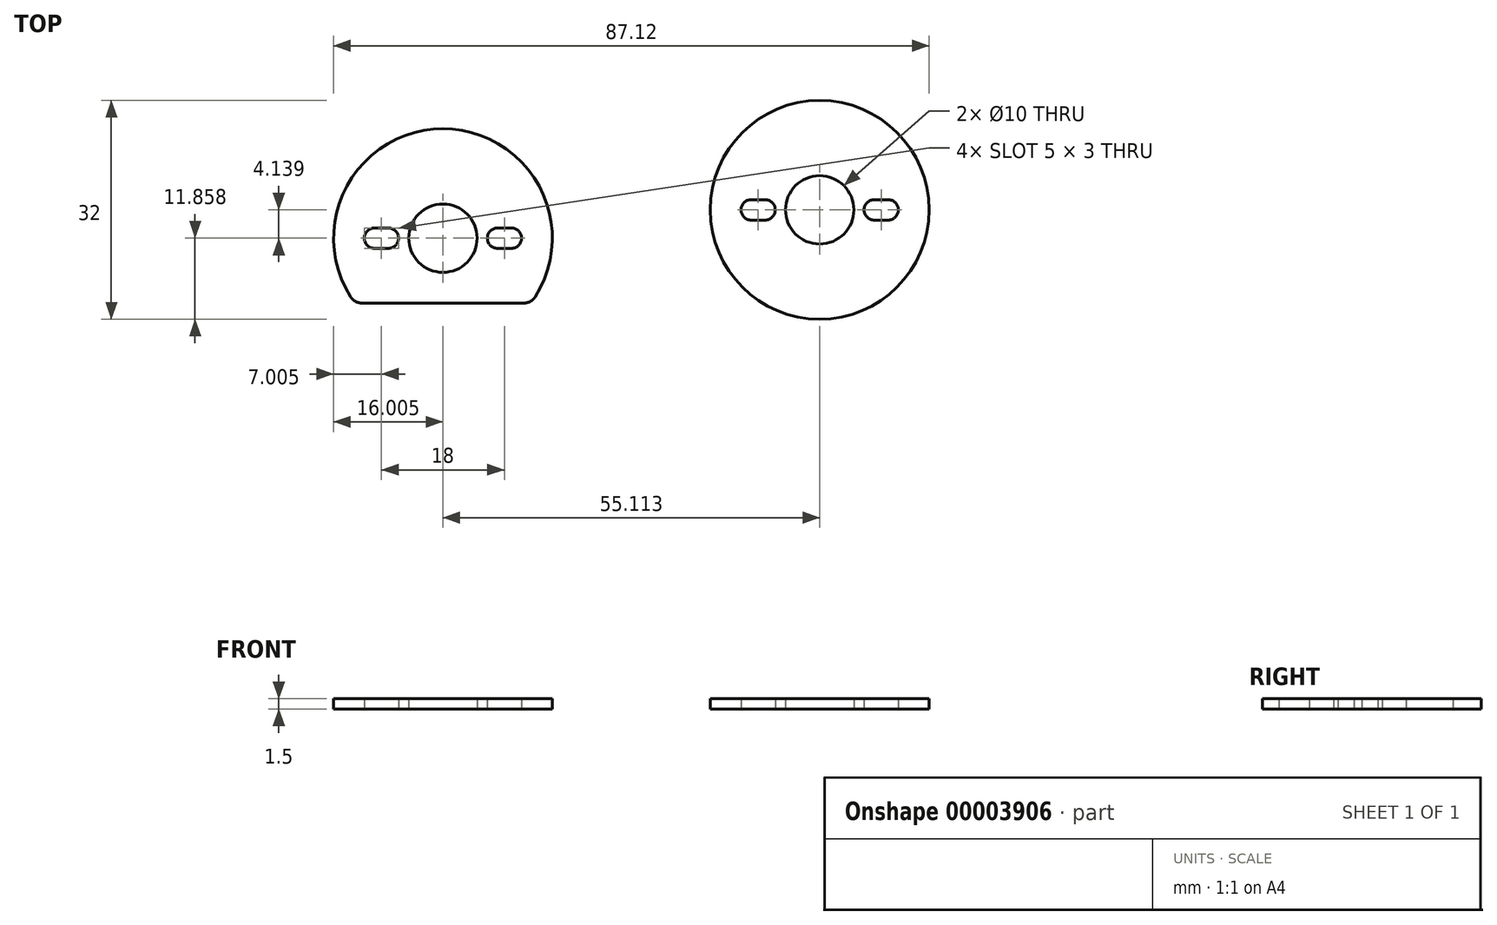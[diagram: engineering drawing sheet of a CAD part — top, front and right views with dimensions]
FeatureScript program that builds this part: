
annotation { "Feature Type Name" : "Feature", "Feature Type Description" : "" }
export const myFeature = defineFeature(function(context is Context, id is Id, definition is map)
    precondition{}
    {
        {
            var Q0;
            Q0=qCreatedBy(makeId("Top.planeOp"),FACE);
            var sketch = newSketch(context, id + "F0", { "sketchPlane" : qUnion([Q0])});
            skCircle(sketch, "E0", {"center": v(-43.17, 52.27) * mm, "radius": 5 * mm});
            skCircle(sketch, "E1", {"center": v(-35.17, 52.27) * mm, "radius": 1.5 * mm});
            skCircle(sketch, "E2", {"center": v(-33.17, 52.27) * mm, "radius": 1.5 * mm});
            skCircle(sketch, "E3", {"center": v(-51.17, 52.27) * mm, "radius": 1.5 * mm});
            skCircle(sketch, "E4", {"center": v(-53.17, 52.27) * mm, "radius": 1.5 * mm});
            skLineSegment(sketch, "E5", {"start": v(-31.41, 53.77) * mm, "end": v(-37.4, 53.77) * mm});
            skLineSegment(sketch, "E6", {"start": v(-36.75, 50.77) * mm, "end": v(-31.2, 50.77) * mm});
            skLineSegment(sketch, "E7", {"start": v(-49.7, 50.77) * mm, "end": v(-55.41, 50.77) * mm});
            skLineSegment(sketch, "E8", {"start": v(-55.27, 53.77) * mm, "end": v(-48.63, 53.77) * mm});
            skLineSegment(sketch, "E9", {"start": v(-54.99, 42.77) * mm, "end": v(-31.34, 42.77) * mm});
            skArc(sketch, "E10", {"start": v(-29.66, 43.7) * mm, "mid": v(-43.17, 68.27) * mm, "end": v(-56.68, 43.7) * mm});
            skArc(sketch, "E11.filletArc", {"start": v(-56.68, 43.7) * mm, "mid": v(-55.95, 43.02) * mm, "end": v(-54.99, 42.77) * mm});
            skArc(sketch, "E12.filletArc", {"start": v(-31.34, 42.77) * mm, "mid": v(-30.38, 43.02) * mm, "end": v(-29.66, 43.7) * mm});
            skSolve(sketch);
        }
        {
            var Q0;
            Q0=makeQuery(id+"F0.imprint","IMPRINT",FACE,{"disambiguationData":[TD([[makeQuery(id+"F0.imprint","IMPRINT",EDGE,{"derivedFrom":sQuery(id+"F0.wireOp",EDGE,"E0")}),-1.0]])]});
            extrude(context, id + "F1", {"entities" : qUnion([Q0]), "depth" : 1.5 * mm});
        }
        {
            var Q0;
            Q0=qCreatedBy(makeId("Top.planeOp"),FACE);
            var sketch = newSketch(context, id + "F2", { "sketchPlane" : qUnion([Q0])});
            skCircle(sketch, "E13", {"center": v(11.95, 56.4) * mm, "radius": 5 * mm});
            skArc(sketch, "E14", {"start": v(-1.56, 64.98) * mm, "mid": v(-2.98, 50.64) * mm, "end": v(7.7, 40.98) * mm});
            skArc(sketch, "E15", {"start": v(16.19, 40.98) * mm, "mid": v(26.87, 50.64) * mm, "end": v(25.46, 64.98) * mm});
            skLineSegment(sketch, "E16", {"start": v(15.66, 40.9) * mm, "end": v(8.24, 40.9) * mm});
            skLineSegment(sketch, "E17", {"start": v(0.13, 65.9) * mm, "end": v(23.77, 65.9) * mm});
            skCircle(sketch, "E18", {"center": v(19.95, 56.4) * mm, "radius": 1.5 * mm});
            skCircle(sketch, "E19", {"center": v(21.95, 56.4) * mm, "radius": 1.5 * mm});
            skCircle(sketch, "E20", {"center": v(3.95, 56.4) * mm, "radius": 1.5 * mm});
            skCircle(sketch, "E21", {"center": v(1.95, 56.4) * mm, "radius": 1.5 * mm});
            skLineSegment(sketch, "E22", {"start": v(5.76, 57.9) * mm, "end": v(0.25, 57.9) * mm});
            skLineSegment(sketch, "E23", {"start": v(-1.08, 54.9) * mm, "end": v(6.26, 54.9) * mm});
            skLineSegment(sketch, "E24", {"start": v(18.24, 57.9) * mm, "end": v(24.37, 57.9) * mm});
            skLineSegment(sketch, "E25", {"start": v(24.22, 54.9) * mm, "end": v(18.62, 54.9) * mm});
            skPoint(sketch, "E26.visualSharp", {"position": v(-0.93, 65.9) * mm});
            skArc(sketch, "E26.filletArc", {"start": v(0.13, 65.9) * mm, "mid": v(-0.84, 65.66) * mm, "end": v(-1.56, 64.98) * mm});
            skPoint(sketch, "E27.visualSharp", {"position": v(24.82, 65.9) * mm});
            skArc(sketch, "E27.filletArc", {"start": v(25.46, 64.98) * mm, "mid": v(24.73, 65.66) * mm, "end": v(23.77, 65.9) * mm});
            skPoint(sketch, "E28.visualSharp", {"position": v(15.92, 40.9) * mm});
            skArc(sketch, "E28.filletArc", {"start": v(15.66, 40.9) * mm, "mid": v(15.92, 40.93) * mm, "end": v(16.19, 40.98) * mm});
            skPoint(sketch, "E29.visualSharp", {"position": v(7.98, 40.9) * mm});
            skArc(sketch, "E29.filletArc", {"start": v(7.7, 40.98) * mm, "mid": v(7.97, 40.93) * mm, "end": v(8.24, 40.9) * mm});
            skCircle(sketch, "E30", {"center": v(11.95, 56.4) * mm, "radius": 16 * mm});
            skSolve(sketch);
        }
        {
            var Q0;
            Q0 = qSketchRegion(id + "F2", true);
            extrude(context, id + "F3", {"entities" : qUnion([Q0]), "depth" : 1.5 * mm});
        }
    });
